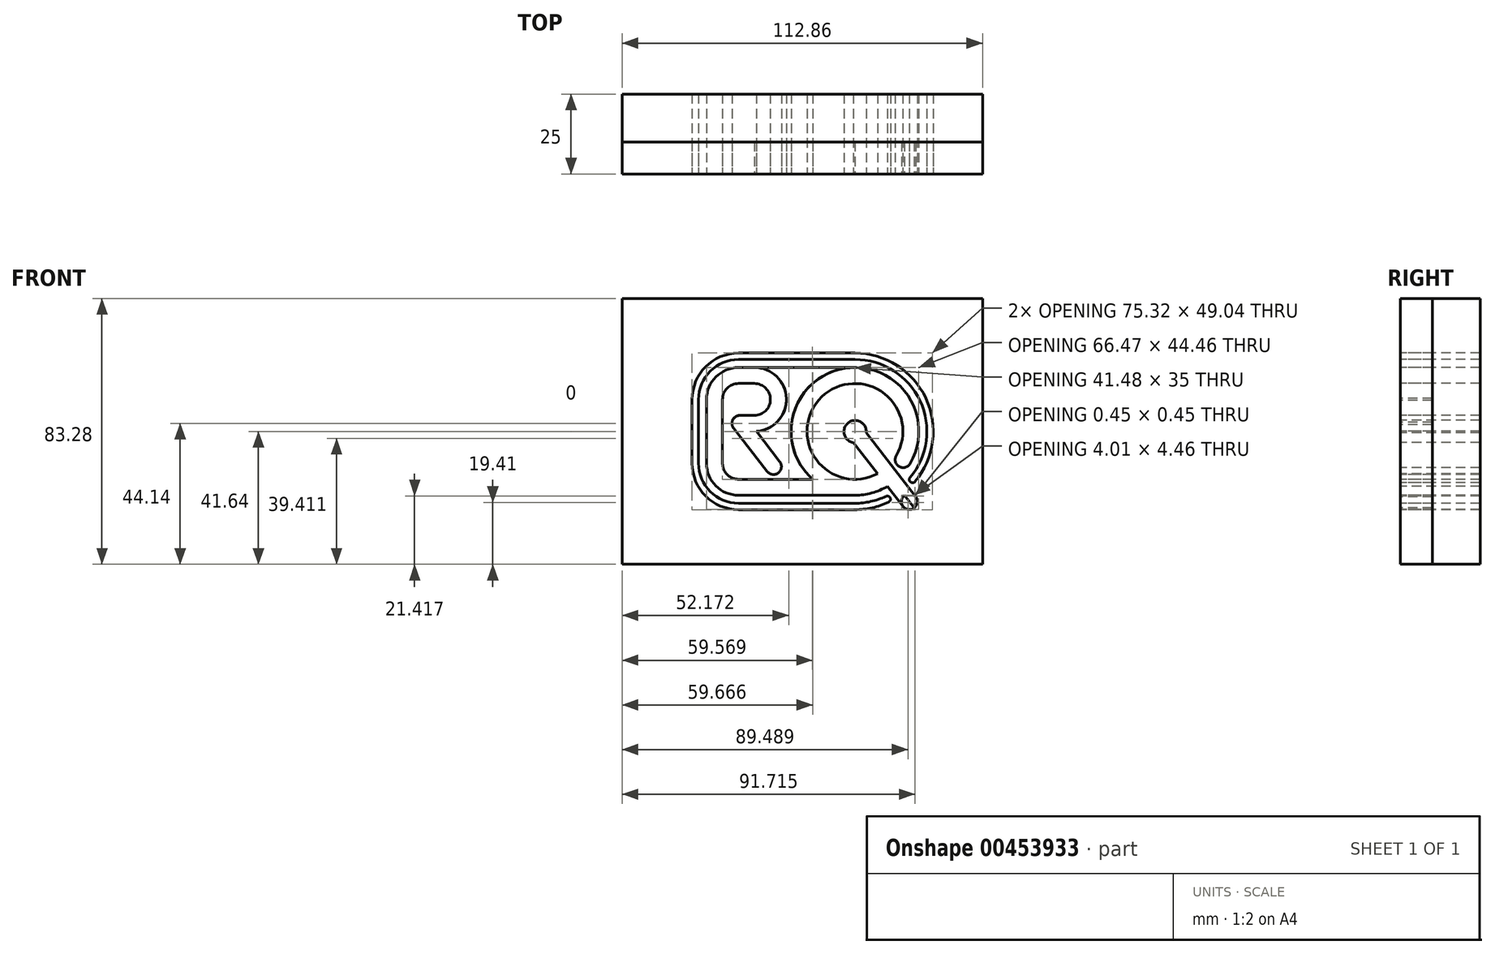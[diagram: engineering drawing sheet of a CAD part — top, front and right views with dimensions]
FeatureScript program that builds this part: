
annotation { "Feature Type Name" : "Feature", "Feature Type Description" : "" }
export const myFeature = defineFeature(function(context is Context, id is Id, definition is map)
    precondition{}
    {
        {
            var Q0;
            Q0=qCreatedBy(makeId("Front.planeOp"),FACE);
            var sketch = newSketch(context, id + "F0", { "sketchPlane" : qUnion([Q0])});
            skPoint(sketch, "E0.middle", {"position": v(0, 0) * mm});
            skLineSegment(sketch, "E1", {"start": v(-25, 10) * mm, "end": v(-25, -10) * mm});
            skLineSegment(sketch, "E2", {"start": v(-25, 20) * mm, "end": v(-15, 20) * mm});
            skLineSegment(sketch, "E3", {"start": v(-21, 0) * mm, "end": v(-15, 0) * mm, "construction": true});
            skLineSegment(sketch, "E4", {"start": v(-5, 10.33) * mm, "end": v(-5, 10.33) * mm});
            skPoint(sketch, "E5.visualSharp", {"position": v(-5.33, 20) * mm});
            skArc(sketch, "E5.filletArc", {"start": v(-5, 10.33) * mm, "mid": v(-8.05, 17.19) * mm, "end": v(-15, 20) * mm});
            skArc(sketch, "E6.filletArc", {"start": v(-15, 0) * mm, "mid": v(-7.81, 3.05) * mm, "end": v(-5, 10.33) * mm});
            skPoint(sketch, "E7.visualSharp", {"position": v(-2, 20) * mm});
            skArc(sketch, "E8.1", {"start": v(-15, 5) * mm, "mid": v(-11.44, 6.5) * mm, "end": v(-10, 10.08) * mm});
            skArc(sketch, "E8.2", {"start": v(-10, 10.08) * mm, "mid": v(-11.5, 13.56) * mm, "end": v(-15, 15) * mm});
            skLineSegment(sketch, "E8.3", {"start": v(-20, 15) * mm, "end": v(-15, 15) * mm});
            skLineSegment(sketch, "E9.0", {"start": v(-30, 17.5) * mm, "end": v(-30, -10) * mm});
            skLineSegment(sketch, "E10.0", {"start": v(-20, -15) * mm, "end": v(0, -14.99) * mm});
            skLineSegment(sketch, "E11", {"start": v(-5, 10.33) * mm, "end": v(-5, 9.67) * mm});
            skPoint(sketch, "E12.newPointB", {"position": v(-23.5, -13.5) * mm});
            skPoint(sketch, "E13.visualSharp", {"position": v(-30, -20) * mm});
            skArc(sketch, "E13.filletArc", {"start": v(-30, -19.5) * mm, "mid": v(-29.85, -19.85) * mm, "end": v(-29.5, -20) * mm});
            skLineSegment(sketch, "E14", {"start": v(-7.29, -12.76) * mm, "end": v(-7.29, -12.76) * mm});
            skArc(sketch, "E15.filletArc", {"start": v(-7.29, -12.76) * mm, "mid": v(-6.55, -11) * mm, "end": v(-7.28, -9.23) * mm});
            skArc(sketch, "E16.filletArc", {"start": v(-11.24, -12.2) * mm, "mid": v(-9.4, -13.47) * mm, "end": v(-7.29, -12.76) * mm});
            skPoint(sketch, "E17.newPointB", {"position": v(-25, 20) * mm});
            skPoint(sketch, "E18.visualSharp", {"position": v(-23.5, 5) * mm});
            skPoint(sketch, "E19.visualSharp", {"position": v(-23.5, 0) * mm});
            skLineSegment(sketch, "E20", {"start": v(-30, 10) * mm, "end": v(-30, 17.5) * mm});
            skLineSegment(sketch, "E21", {"start": v(-20, 20) * mm, "end": v(-25, 20) * mm});
            skPoint(sketch, "E22.visualSharp", {"position": v(-30, 20) * mm});
            skArc(sketch, "E22.filletArc", {"start": v(-20, 20) * mm, "mid": v(-27.07, 17.07) * mm, "end": v(-30, 10) * mm});
            skPoint(sketch, "E23.newPointB", {"position": v(-25, -20) * mm});
            skArc(sketch, "E23.filletArc", {"start": v(-25, -10) * mm, "mid": v(-23.53, -13.54) * mm, "end": v(-20, -15) * mm});
            skLineSegment(sketch, "E24", {"start": v(-15, 20) * mm, "end": v(8, 20) * mm});
            skLineSegment(sketch, "E25", {"start": v(16.48, -24.52) * mm, "end": v(-20, -24.52) * mm});
            skLineSegment(sketch, "E26", {"start": v(13, 24.52) * mm, "end": v(-20, 24.52) * mm});
            skLineSegment(sketch, "E27", {"start": v(-34.52, -10) * mm, "end": v(-34.52, 10) * mm});
            skLineSegment(sketch, "E28.0", {"start": v(-32.52, -10) * mm, "end": v(-32.52, 10) * mm});
            skLineSegment(sketch, "E29.0", {"start": v(13, 22.52) * mm, "end": v(-20, 22.52) * mm});
            skPoint(sketch, "E30.visualSharp", {"position": v(-32.52, 22.52) * mm});
            skArc(sketch, "E30.filletArc", {"start": v(-20, 22.52) * mm, "mid": v(-28.85, 18.85) * mm, "end": v(-32.52, 10) * mm});
            skArc(sketch, "E31.0", {"start": v(-20, 24.52) * mm, "mid": v(-30.27, 20.27) * mm, "end": v(-34.52, 10) * mm});
            skPoint(sketch, "E32.visualSharp", {"position": v(-32.52, -22.52) * mm});
            skLineSegment(sketch, "E33.trimOffspring", {"start": v(16.48, -22.52) * mm, "end": v(-20, -22.52) * mm});
            skLineSegment(sketch, "E34.bottom", {"start": v(-56.43, 41.64) * mm, "end": v(56.43, 41.64) * mm});
            skLineSegment(sketch, "E34.top", {"start": v(-56.43, -41.64) * mm, "end": v(56.43, -41.64) * mm});
            skLineSegment(sketch, "E34.left", {"start": v(-56.43, 41.64) * mm, "end": v(-56.43, -41.64) * mm});
            skLineSegment(sketch, "E34.right", {"start": v(56.43, 41.64) * mm, "end": v(56.43, -41.64) * mm});
            skLineSegment(sketch, "E35", {"start": v(0, 0) * mm, "end": v(0, -38.7) * mm, "construction": true});
            skLineSegment(sketch, "E36", {"start": v(0, 0) * mm, "end": v(33.56, 0) * mm, "construction": true});
            skArc(sketch, "E37.filletArc", {"start": v(-20, 15) * mm, "mid": v(-23.54, 13.54) * mm, "end": v(-25, 10) * mm});
            skArc(sketch, "E38.0", {"start": v(-30, -10) * mm, "mid": v(-27.07, -17.07) * mm, "end": v(-20, -20) * mm});
            skArc(sketch, "E39.0", {"start": v(-34.52, -10) * mm, "mid": v(-30.27, -20.27) * mm, "end": v(-20, -24.52) * mm});
            skArc(sketch, "E40.0", {"start": v(-32.52, -10) * mm, "mid": v(-28.85, -18.85) * mm, "end": v(-20, -22.52) * mm});
            skLineSegment(sketch, "E41", {"start": v(-15, 5) * mm, "end": v(-21, 5) * mm});
            skLineSegment(sketch, "E42", {"start": v(-23.5, 2.5) * mm, "end": v(-23.5, 2.5) * mm});
            skPoint(sketch, "E43.startSnap0", {"position": v(-6.55, -11) * mm});
            skLineSegment(sketch, "E44", {"start": v(-22, 7.18) * mm, "end": v(-22, -5.45) * mm});
            skArc(sketch, "E45", {"start": v(-19.53, 5) * mm, "mid": v(-22.03, 2.5) * mm, "end": v(-19.53, 0) * mm});
            skLineSegment(sketch, "E46", {"start": v(-21.5, 0.97) * mm, "end": v(-11.03, -12.53) * mm});
            skLineSegment(sketch, "E47.0", {"start": v(-17.54, 4.02) * mm, "end": v(-7.07, -9.47) * mm});
            skLineSegment(sketch, "E48", {"start": v(30.79, -22.52) * mm, "end": v(75.8, -22.52) * mm});
            skLineSegment(sketch, "E49", {"start": v(8, 20) * mm, "end": v(76.58, 20) * mm});
            skArc(sketch, "E50.0", {"start": v(28.5, -8.97) * mm, "mid": v(28.6, -8.83) * mm, "end": v(28.71, -8.7) * mm});
            skLineSegment(sketch, "E51", {"start": v(16.47, 0) * mm, "end": v(16.53, -0.06) * mm, "construction": true});
            skLineSegment(sketch, "E52", {"start": v(32, -20) * mm, "end": v(32, -20) * mm});
            skCircle(sketch, "E53", {"center": v(16.47, 0) * mm, "radius": 2.5 * mm});
            skLineSegment(sketch, "E54", {"start": v(-20, -20) * mm, "end": v(16.48, -20) * mm});
            skArc(sketch, "E55", {"start": v(33.75, -10.1) * mm, "mid": v(13.32, 19.75) * mm, "end": v(3.24, -14.99) * mm});
            skLineSegment(sketch, "E56", {"start": v(0, -14.99) * mm, "end": v(3.24, -14.99) * mm});
            skLineSegment(sketch, "E57", {"start": v(-17.54, 4.02) * mm, "end": v(-17.54, 0.98) * mm});
            skLineSegment(sketch, "E58", {"start": v(16.48, 0) * mm, "end": v(37.68, -27.32) * mm});
            skCircle(sketch, "E59", {"center": v(33.53, -21.98) * mm, "radius": 2.5 * mm});
            skLineSegment(sketch, "E60", {"start": v(31.56, -23.51) * mm, "end": v(14.49, -1.54) * mm});
            skLineSegment(sketch, "E61", {"start": v(35.5, -20.45) * mm, "end": v(18.45, 1.54) * mm});
            skCircle(sketch, "E62", {"center": v(31.59, -8.84) * mm, "radius": 2.5 * mm});
            skArc(sketch, "E63.trimOffspring", {"start": v(29.43, -7.58) * mm, "mid": v(6.08, 10.8) * mm, "end": v(23.57, -13.22) * mm});
            skArc(sketch, "E64.0", {"start": v(35.92, -11.37) * mm, "mid": v(36.02, 11.2) * mm, "end": v(16.48, 22.52) * mm});
            skLineSegment(sketch, "E65", {"start": v(13, 22.52) * mm, "end": v(16.48, 22.52) * mm});
            skArc(sketch, "E66.0", {"start": v(37.65, -12.38) * mm, "mid": v(37.76, 12.2) * mm, "end": v(16.48, 24.52) * mm});
            skLineSegment(sketch, "E67", {"start": v(13, 24.52) * mm, "end": v(16.48, 24.52) * mm});
            skArc(sketch, "E68.trimOffspring", {"start": v(16.48, -24.52) * mm, "mid": v(21.9, -23.92) * mm, "end": v(27.04, -22.13) * mm});
            skArc(sketch, "E69.trimOffspring", {"start": v(-0.32, -14.99) * mm, "mid": v(-0.16, -15.17) * mm, "end": v(0, -15.34) * mm});
            skPoint(sketch, "E70.trimOffspring.end.orphan", {"position": v(-5, 0) * mm});
            skArc(sketch, "E71.trimOffspring", {"start": v(16.48, -22.52) * mm, "mid": v(21.46, -21.96) * mm, "end": v(26.18, -20.33) * mm});
            skArc(sketch, "E72.trimOffspring", {"start": v(16.48, -20) * mm, "mid": v(21.76, -19.3) * mm, "end": v(26.67, -17.21) * mm});
            skLineSegment(sketch, "E73.trimOffspring", {"start": v(35.06, -20) * mm, "end": v(35.16, -20) * mm});
            skLineSegment(sketch, "E74.0", {"start": v(33.73, -15.7) * mm, "end": v(33.73, -15.7) * mm});
            skArc(sketch, "E75", {"start": v(33.75, -14.45) * mm, "mid": v(36.89, 9.53) * mm, "end": v(16.48, 22.52) * mm});
            skArc(sketch, "E76", {"start": v(35.29, -15.74) * mm, "mid": v(38.7, 10.38) * mm, "end": v(16.48, 24.52) * mm});
            skCircle(sketch, "E77", {"center": v(26.61, -21.23) * mm, "radius": 1 * mm});
            skArc(sketch, "E78.filletArc", {"start": v(33.75, -14.45) * mm, "mid": v(33.52, -15.08) * mm, "end": v(33.73, -15.7) * mm});
            skArc(sketch, "E79.filletArc", {"start": v(33.73, -15.7) * mm, "mid": v(34.5, -16.1) * mm, "end": v(35.29, -15.74) * mm});
            skCircle(sketch, "E80", {"center": v(16.53, -0.06) * mm, "radius": 3.5 * mm});
            skLineSegment(sketch, "E81.bottom", {"start": v(76.15, 50.71) * mm, "end": v(-76.15, 50.71) * mm});
            skLineSegment(sketch, "E81.top", {"start": v(76.15, -50.71) * mm, "end": v(-76.15, -50.71) * mm});
            skLineSegment(sketch, "E81.left", {"start": v(76.15, 50.71) * mm, "end": v(76.15, -50.71) * mm});
            skLineSegment(sketch, "E81.right", {"start": v(-76.15, 50.71) * mm, "end": v(-76.15, -50.71) * mm});
            skSolve(sketch);
        }
        {
            var Q0;
            Q0=makeQuery(id+"F0.imprint","IMPRINT",FACE,{"disambiguationData":[TD([[makeQuery(id+"F0.imprint","IMPRINT",EDGE,{"derivedFrom":sQuery(id+"F0.wireOp",EDGE,"E1")}),-1.0]])]});
            var Q1;
            {var subQ5=sQuery(id+"F0.wireOp",EDGE,"E60");var subQ6=sQuery(id+"F0.wireOp",EDGE,"E50.0");var subQ7=makeQuery(id+"F0.imprint","INTERSECT",VERTEX,{"derivedFrom":[subQ6,subQ5]});Q1=makeQuery(id+"F0.imprint","IMPRINT",FACE,{"disambiguationData":[TD([[makeQuery(id+"F0.imprint","IMPRINT",EDGE,{"disambiguationData":[TD([[subQ7,1.0]])],"derivedFrom":subQ6}),-1.0]])]});}
            var Q2;
            {var subQ0=sQuery(id+"F0.wireOp",EDGE,"E60");var subQ1=sQuery(id+"F0.wireOp",EDGE,"E52");var subQ2=makeQuery(id+"F0.imprint","INTERSECT",VERTEX,{"derivedFrom":[subQ1,subQ0]});Q2=makeQuery(id+"F0.imprint","IMPRINT",FACE,{"disambiguationData":[TD([[makeQuery(id+"F0.imprint","IMPRINT",EDGE,{"disambiguationData":[TD([[subQ2,-1.0]])],"derivedFrom":subQ1}),1.0]])]});}
            var Q3;
            {var subQ0=sQuery(id+"F0.wireOp",EDGE,"E58");var subQ1=sQuery(id+"F0.wireOp",EDGE,"E52");var subQ2=makeQuery(id+"F0.imprint","INTERSECT",VERTEX,{"derivedFrom":[subQ1,subQ0]});Q3=makeQuery(id+"F0.imprint","IMPRINT",FACE,{"disambiguationData":[TD([[makeQuery(id+"F0.imprint","IMPRINT",EDGE,{"disambiguationData":[TD([[subQ2,-1.0]])],"derivedFrom":subQ1}),1.0]])]});}
            var Q4;
            {var subQ0=sQuery(id+"F0.wireOp",EDGE,"E58");var subQ1=sQuery(id+"F0.wireOp",EDGE,"E50.0");var subQ2=makeQuery(id+"F0.imprint","INTERSECT",VERTEX,{"derivedFrom":[subQ1,subQ0]});Q4=makeQuery(id+"F0.imprint","IMPRINT",FACE,{"disambiguationData":[TD([[makeQuery(id+"F0.imprint","IMPRINT",EDGE,{"disambiguationData":[TD([[subQ2,1.0]])],"derivedFrom":subQ1}),-1.0]])]});}
            var Q5;
            {var subQ0=sQuery(id+"F0.wireOp",EDGE,"E58");var subQ1=sQuery(id+"F0.wireOp",EDGE,"E50.0");var subQ2=makeQuery(id+"F0.imprint","INTERSECT",VERTEX,{"derivedFrom":[subQ1,subQ0]});Q5=makeQuery(id+"F0.imprint","IMPRINT",FACE,{"disambiguationData":[TD([[makeQuery(id+"F0.imprint","IMPRINT",EDGE,{"disambiguationData":[TD([[subQ2,-1.0]])],"derivedFrom":subQ1}),-1.0]])]});}
            var Q6;
            {var subQ1=sQuery(id+"F0.wireOp",EDGE,"E48");var subQ7=sQuery(id+"F0.wireOp",EDGE,"E60");var subQ9=makeQuery(id+"F0.imprint","INTERSECT",VERTEX,{"derivedFrom":[subQ1,subQ7]});Q6=makeQuery(id+"F0.imprint","IMPRINT",FACE,{"disambiguationData":[TD([[makeQuery(id+"F0.imprint","IMPRINT",EDGE,{"disambiguationData":[TD([[subQ9,-1.0]])],"derivedFrom":subQ1}),1.0]])]});}
            var Q7;
            {var subQ4=sQuery(id+"F0.wireOp",EDGE,"E58");var subQ5=sQuery(id+"F0.wireOp",EDGE,"E48");var subQ6=makeQuery(id+"F0.imprint","INTERSECT",VERTEX,{"derivedFrom":[subQ5,subQ4]});Q7=makeQuery(id+"F0.imprint","IMPRINT",FACE,{"disambiguationData":[TD([[makeQuery(id+"F0.imprint","IMPRINT",EDGE,{"disambiguationData":[TD([[subQ6,-1.0]])],"derivedFrom":subQ5}),1.0]])]});}
            var Q8;
            {var subQ0=sQuery(id+"F0.wireOp",EDGE,"E59");var subQ1=sQuery(id+"F0.wireOp",EDGE,"E52");var subQ2=makeQuery(id+"F0.imprint","INTERSECT",VERTEX,{"disambiguationData":[OD(0.0)],"derivedFrom":[subQ1,subQ0]});Q8=makeQuery(id+"F0.imprint","IMPRINT",FACE,{"disambiguationData":[TD([[makeQuery(id+"F0.imprint","IMPRINT",EDGE,{"disambiguationData":[TD([[subQ2,-1.0]])],"derivedFrom":subQ1}),1.0]])]});}
            var Q9;
            {var subQ0=sQuery(id+"F0.wireOp",EDGE,"E59");var subQ1=sQuery(id+"F0.wireOp",EDGE,"E48");var subQ2=makeQuery(id+"F0.imprint","INTERSECT",VERTEX,{"disambiguationData":[OD(0.0)],"derivedFrom":[subQ1,subQ0]});Q9=makeQuery(id+"F0.imprint","IMPRINT",FACE,{"disambiguationData":[TD([[makeQuery(id+"F0.imprint","IMPRINT",EDGE,{"disambiguationData":[TD([[subQ2,-1.0]])],"derivedFrom":subQ1}),1.0]])]});}
            var Q10;
            {var subQ0=sQuery(id+"F0.wireOp",EDGE,"E60");var subQ1=sQuery(id+"F0.wireOp",EDGE,"E48");var subQ2=makeQuery(id+"F0.imprint","INTERSECT",VERTEX,{"derivedFrom":[subQ1,subQ0]});Q10=makeQuery(id+"F0.imprint","IMPRINT",FACE,{"disambiguationData":[TD([[makeQuery(id+"F0.imprint","IMPRINT",EDGE,{"disambiguationData":[TD([[subQ2,-1.0]])],"derivedFrom":subQ1}),-1.0]])]});}
            var Q11;
            {var subQ0=sQuery(id+"F0.wireOp",EDGE,"E59");var subQ1=sQuery(id+"F0.wireOp",EDGE,"E48");var subQ2=makeQuery(id+"F0.imprint","INTERSECT",VERTEX,{"disambiguationData":[OD(0.0)],"derivedFrom":[subQ1,subQ0]});Q11=makeQuery(id+"F0.imprint","IMPRINT",FACE,{"disambiguationData":[TD([[makeQuery(id+"F0.imprint","IMPRINT",EDGE,{"disambiguationData":[TD([[subQ2,-1.0]])],"derivedFrom":subQ1}),-1.0]])]});}
            var Q12;
            {var subQ0=sQuery(id+"F0.wireOp",EDGE,"E58");var subQ1=sQuery(id+"F0.wireOp",EDGE,"E48");var subQ2=makeQuery(id+"F0.imprint","INTERSECT",VERTEX,{"derivedFrom":[subQ1,subQ0]});Q12=makeQuery(id+"F0.imprint","IMPRINT",FACE,{"disambiguationData":[TD([[makeQuery(id+"F0.imprint","IMPRINT",EDGE,{"disambiguationData":[TD([[subQ2,-1.0]])],"derivedFrom":subQ1}),-1.0]])]});}
            var Q13;
            {var subQ0=sQuery(id+"F0.wireOp",EDGE,"E59");var subQ1=sQuery(id+"F0.wireOp",EDGE,"E52");var subQ2=makeQuery(id+"F0.imprint","INTERSECT",VERTEX,{"disambiguationData":[OD(1.0)],"derivedFrom":[subQ1,subQ0]});Q13=makeQuery(id+"F0.imprint","IMPRINT",FACE,{"disambiguationData":[TD([[makeQuery(id+"F0.imprint","IMPRINT",EDGE,{"disambiguationData":[TD([[subQ2,-1.0]])],"derivedFrom":subQ1}),-1.0]])]});}
            var Q14;
            {var subQ0=sQuery(id+"F0.wireOp",EDGE,"E53");var subQ1=makeQuery(id+"F0.imprint","INTERSECT",VERTEX,{"derivedFrom":[subQ0,sQuery(id+"F0.wireOp",EDGE,"E60")]});Q14=makeQuery(id+"F0.imprint","IMPRINT",FACE,{"disambiguationData":[TD([[makeQuery(id+"F0.imprint","IMPRINT",EDGE,{"disambiguationData":[TD([[subQ1,1.0]])],"derivedFrom":subQ0}),1.0]])]});}
            var Q15;
            {var subQ0=sQuery(id+"F0.wireOp",EDGE,"E58");var subQ1=sQuery(id+"F0.wireOp",EDGE,"E50.0");var subQ2=makeQuery(id+"F0.imprint","INTERSECT",VERTEX,{"derivedFrom":[subQ1,subQ0]});Q15=makeQuery(id+"F0.imprint","IMPRINT",FACE,{"disambiguationData":[TD([[makeQuery(id+"F0.imprint","IMPRINT",EDGE,{"disambiguationData":[TD([[subQ2,1.0]])],"derivedFrom":subQ1}),1.0]])]});}
            var Q16;
            {var subQ0=sQuery(id+"F0.wireOp",EDGE,"E58");var subQ1=sQuery(id+"F0.wireOp",EDGE,"E50.0");var subQ2=makeQuery(id+"F0.imprint","INTERSECT",VERTEX,{"derivedFrom":[subQ1,subQ0]});Q16=makeQuery(id+"F0.imprint","IMPRINT",FACE,{"disambiguationData":[TD([[makeQuery(id+"F0.imprint","IMPRINT",EDGE,{"disambiguationData":[TD([[subQ2,-1.0]])],"derivedFrom":subQ1}),1.0]])]});}
            var Q17;
            {var subQ0=sQuery(id+"F0.wireOp",EDGE,"E55");var subQ9=makeQuery(id+"F0.imprint","INTERSECT",VERTEX,{"derivedFrom":[sQuery(id+"F0.wireOp",EDGE,"p0NgMthc-pwGy-uEBE-NfGK-XhEp5236UaCg"),subQ0]});Q17=makeQuery(id+"F0.imprint","IMPRINT",FACE,{"disambiguationData":[TD([[makeQuery(id+"F0.imprint","IMPRINT",EDGE,{"disambiguationData":[TD([[subQ9,1.0]])],"derivedFrom":subQ0}),1.0]])]});}
            var Q18;
            {var subQ0=sQuery(id+"F0.wireOp",EDGE,"E62");var subQ1=makeQuery(id+"F0.imprint","INTERSECT",VERTEX,{"derivedFrom":[sQuery(id+"F0.wireOp",EDGE,"E55"),subQ0]});Q18=makeQuery(id+"F0.imprint","IMPRINT",FACE,{"disambiguationData":[TD([[makeQuery(id+"F0.imprint","IMPRINT",EDGE,{"disambiguationData":[TD([[subQ1,1.0]])],"derivedFrom":subQ0}),1.0]])]});}
            var Q19;
            {var subQ0=sQuery(id+"F0.wireOp",EDGE,"E58");var subQ1=sQuery(id+"F0.wireOp",EDGE,"E55");var subQ2=makeQuery(id+"F0.imprint","INTERSECT",VERTEX,{"derivedFrom":[subQ1,subQ0]});Q19=makeQuery(id+"F0.imprint","IMPRINT",FACE,{"disambiguationData":[TD([[makeQuery(id+"F0.imprint","IMPRINT",EDGE,{"disambiguationData":[TD([[subQ2,-1.0]])],"derivedFrom":subQ1}),1.0]])]});}
            var Q20;
            {var subQ0=sQuery(id+"F0.wireOp",EDGE,"E60");var subQ1=sQuery(id+"F0.wireOp",EDGE,"E55");var subQ2=makeQuery(id+"F0.imprint","INTERSECT",VERTEX,{"derivedFrom":[subQ1,subQ0]});Q20=makeQuery(id+"F0.imprint","IMPRINT",FACE,{"disambiguationData":[TD([[makeQuery(id+"F0.imprint","IMPRINT",EDGE,{"disambiguationData":[TD([[subQ2,-1.0]])],"derivedFrom":subQ1}),1.0]])]});}
            var Q21;
            {var subQ0=sQuery(id+"F0.wireOp",EDGE,"E61");var subQ1=sQuery(id+"F0.wireOp",EDGE,"E53");var subQ2=makeQuery(id+"F0.imprint","INTERSECT",VERTEX,{"derivedFrom":[subQ1,subQ0]});Q21=makeQuery(id+"F0.imprint","IMPRINT",FACE,{"disambiguationData":[TD([[makeQuery(id+"F0.imprint","IMPRINT",EDGE,{"disambiguationData":[TD([[subQ2,1.0]])],"derivedFrom":subQ1}),-1.0]])]});}
            var Q22;
            {var subQ0=sQuery(id+"F0.wireOp",EDGE,"E60");var subQ1=sQuery(id+"F0.wireOp",EDGE,"E53");var subQ2=makeQuery(id+"F0.imprint","INTERSECT",VERTEX,{"derivedFrom":[subQ1,subQ0]});Q22=makeQuery(id+"F0.imprint","IMPRINT",FACE,{"disambiguationData":[TD([[makeQuery(id+"F0.imprint","IMPRINT",EDGE,{"disambiguationData":[TD([[subQ2,-1.0]])],"derivedFrom":subQ1}),-1.0]])]});}
            var Q23;
            {var subQ0=sQuery(id+"F0.wireOp",EDGE,"E60");var subQ1=sQuery(id+"F0.wireOp",EDGE,"E53");var subQ2=makeQuery(id+"F0.imprint","INTERSECT",VERTEX,{"derivedFrom":[subQ1,subQ0]});Q23=makeQuery(id+"F0.imprint","IMPRINT",FACE,{"disambiguationData":[TD([[makeQuery(id+"F0.imprint","IMPRINT",EDGE,{"disambiguationData":[TD([[subQ2,1.0]])],"derivedFrom":subQ1}),-1.0]])]});}
            extrude(context, id + "F1", {"entities" : qUnion([Q0, Q1, Q2, Q3, Q4, Q5, Q6, Q7, Q8, Q9, Q10, Q11, Q12, Q13, Q14, Q15, Q16, Q17, Q18, Q19, Q20, Q21, Q22, Q23]), "oppositeDirection" : true, "depth" : 10 * mm});
        }
        {
            var Q0;
            {var subQ4=sQuery(id+"F0.wireOp",EDGE,"E78.filletArc");Q0=makeQuery(id+"F0.imprint","IMPRINT",FACE,{"disambiguationData":[TD([[makeQuery(id+"F0.imprint","IMPRINT",EDGE,{"derivedFrom":subQ4}),1.0]])]});}
            var Q1;
            Q1=makeQuery(id+"F0.imprint","IMPRINT",FACE,{"disambiguationData":[TD([[makeQuery(id+"F0.imprint","IMPRINT",EDGE,{"derivedFrom":sQuery(id+"F0.wireOp",EDGE,"E25")}),-1.0]])]});
            var Q2;
            {var subQ0=sQuery(id+"F0.wireOp",EDGE,"E77");var subQ1=makeQuery(id+"F0.imprint","INTERSECT",VERTEX,{"derivedFrom":[sQuery(id+"F0.wireOp",EDGE,"E68.trimOffspring"),subQ0]});Q2=makeQuery(id+"F0.imprint","IMPRINT",FACE,{"disambiguationData":[TD([[makeQuery(id+"F0.imprint","IMPRINT",EDGE,{"disambiguationData":[TD([[subQ1,1.0]])],"derivedFrom":subQ0}),1.0]])]});}
            extrude(context, id + "F2", {"entities" : qUnion([Q0, Q1, Q2]), "oppositeDirection" : true, "depth" : 10 * mm});
        }
        {
            var Q0;
            Q0=makeQuery(id+"F0.imprint","IMPRINT",FACE,{"disambiguationData":[TD([[makeQuery(id+"F0.imprint","IMPRINT",EDGE,{"derivedFrom":sQuery(id+"F0.wireOp",EDGE,"E2")}),1.0]])]});
            var Q1;
            {var subQ3=sQuery(id+"F0.wireOp",EDGE,"E63.trimOffspring");Q1=makeQuery(id+"F0.imprint","IMPRINT",FACE,{"disambiguationData":[TD([[makeQuery(id+"F0.imprint","IMPRINT",EDGE,{"derivedFrom":subQ3}),1.0]])]});}
            var Q2;
            Q2=makeQuery(id+"F0.imprint","IMPRINT",FACE,{"disambiguationData":[TD([[makeQuery(id+"F0.imprint","IMPRINT",EDGE,{"derivedFrom":sQuery(id+"F0.wireOp",EDGE,"E1")}),1.0]])]});
            extrude(context, id + "F3", {"entities" : qUnion([Q0, Q1, Q2]), "oppositeDirection" : true, "depth" : 25 * mm});
        }
    });
